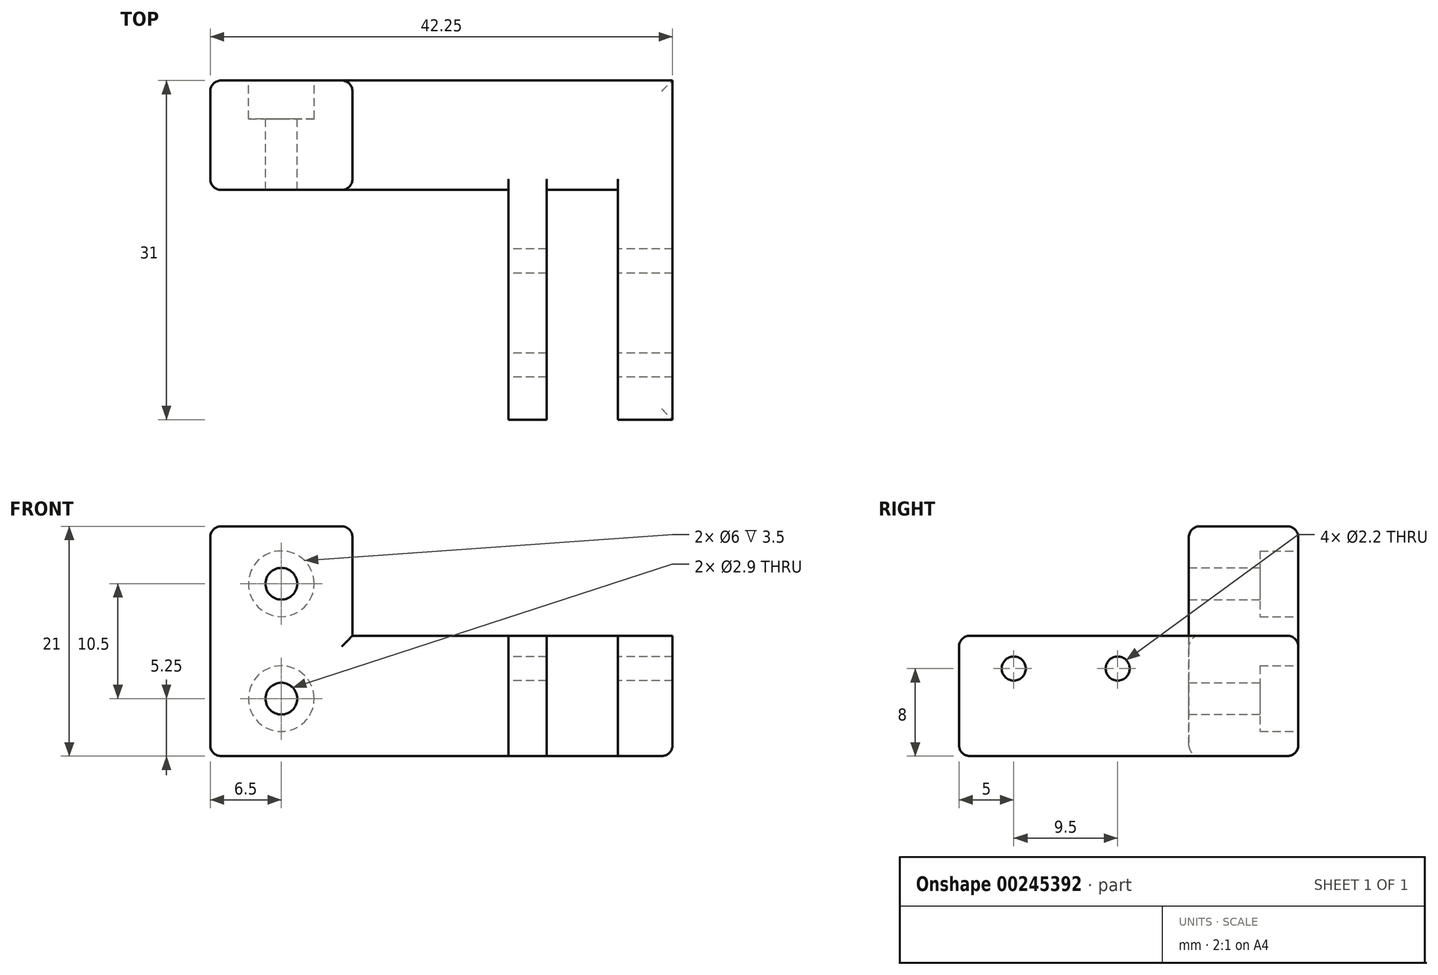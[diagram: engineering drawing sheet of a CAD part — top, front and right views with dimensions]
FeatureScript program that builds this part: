
annotation { "Feature Type Name" : "Feature", "Feature Type Description" : "" }
export const myFeature = defineFeature(function(context is Context, id is Id, definition is map)
    precondition{}
    {
        {
            var Q0;
            Q0=qCreatedBy(makeId("Front.planeOp"),FACE);
            var sketch = newSketch(context, id + "F0", { "sketchPlane" : qUnion([Q0])});
            skLineSegment(sketch, "E0.bottom", {"start": v(0, 0) * mm, "end": v(16.5, 0) * mm});
            skLineSegment(sketch, "E0.top", {"start": v(0, 11) * mm, "end": v(16.5, 11) * mm});
            skLineSegment(sketch, "E0.left", {"start": v(0, 0) * mm, "end": v(0, 11) * mm});
            skLineSegment(sketch, "E0.right", {"start": v(16.5, 0) * mm, "end": v(16.5, 11) * mm});
            skSolve(sketch);
        }
        {
            var Q0;
            Q0=qSketchRegion(id+"F0",true);
            extrude(context, id + "F1", {"entities" : qUnion([Q0]), "depth" : 10 * mm});
        }
        {
            var Q0;
            Q0=makeQuery(id+"F1.opExtrude","CAP_FACE",FACE,{"disambiguationData":[OSD([sQuery(id+"F0.wireOp",EDGE,"E0.bottom"),sQuery(id+"F0.wireOp",EDGE,"E0.top"),sQuery(id+"F0.wireOp",EDGE,"E0.left"),sQuery(id+"F0.wireOp",EDGE,"E0.right")])],"isStart":false});
            var sketch = newSketch(context, id + "F2", { "sketchPlane" : qUnion([Q0])});
            skLineSegment(sketch, "E1.left", {"start": v(11.5, 11) * mm, "end": v(11.5, 0) * mm});
            skLineSegment(sketch, "E1.right", {"start": v(5, 11) * mm, "end": v(5, 0) * mm});
            skPoint(sketch, "E1.middle", {"position": v(8.25, 5.5) * mm});
            skPoint(sketch, "E1.middle.positionSnap0", {"position": v(0, 5.5) * mm});
            skPoint(sketch, "E1.middle.positionSnap1", {"position": v(8.25, 0) * mm});
            skPoint(sketch, "E1.centerSnap0", {"position": v(0, 5.5) * mm});
            skPoint(sketch, "E1.centerSnap1", {"position": v(8.25, 0) * mm});
            skLineSegment(sketch, "E2", {"start": v(5, 11) * mm, "end": v(0, 11) * mm});
            skLineSegment(sketch, "E3", {"start": v(0, 11) * mm, "end": v(0, 0) * mm});
            skLineSegment(sketch, "E4", {"start": v(0, 0) * mm, "end": v(5, 0) * mm});
            skLineSegment(sketch, "E5", {"start": v(11.5, 11) * mm, "end": v(16.5, 11) * mm});
            skLineSegment(sketch, "E6", {"start": v(16.5, 11) * mm, "end": v(16.5, 0) * mm});
            skLineSegment(sketch, "E7", {"start": v(16.5, 0) * mm, "end": v(11.5, 0) * mm});
            skSolve(sketch);
        }
        {
            var Q0;
            Q0=qSketchRegion(id+"F2",true);
            extrude(context, id + "F3", {"entities" : qUnion([Q0]), "operationType" : NewBodyOperationType.ADD, "depth" : 21 * mm});
        }
        {
            var Q0;
            Q0=makeQuery(id+"F3.boolean.opBoolean","MERGE",FACE,{"derivedFrom":[makeQuery(id+"F1.opExtrude","SWEPT_FACE",FACE,{"disambiguationData":[OSD([sQuery(id+"F0.wireOp",EDGE,"E0.left")])]}),makeQuery(id+"F3.opExtrude","SWEPT_FACE",FACE,{"disambiguationData":[OSD([sQuery(id+"F2.wireOp",EDGE,"E3")])]})]});
            var sketch = newSketch(context, id + "F4", { "sketchPlane" : qUnion([Q0])});
            skLineSegment(sketch, "E8", {"start": v(31, 11) * mm, "end": v(31, 8) * mm});
            skLineSegment(sketch, "E9", {"start": v(31, 8) * mm, "end": v(26, 8) * mm});
            skCircle(sketch, "E10", {"center": v(26, 8) * mm, "radius": 1.1 * mm});
            skLineSegment(sketch, "E11", {"start": v(26, 8) * mm, "end": v(16.5, 8) * mm});
            skCircle(sketch, "E12", {"center": v(16.5, 8) * mm, "radius": 1.1 * mm});
            skSolve(sketch);
        }
        {
            var Q0;
            Q0=qSketchRegion(id+"F4",true);
            extrude(context, id + "F5", {"entities" : qUnion([Q0]), "operationType" : NewBodyOperationType.REMOVE, "oppositeDirection" : true, "depth" : 25 * mm});
        }
        {
            var Q0;
            Q0=makeQuery(id+"F3.opExtrude","CAP_FACE",FACE,{"disambiguationData":[OSD([sQuery(id+"F2.wireOp",EDGE,"E1.right"),sQuery(id+"F2.wireOp",EDGE,"E2"),sQuery(id+"F2.wireOp",EDGE,"E3"),sQuery(id+"F2.wireOp",EDGE,"E4")])],"isStart":false});
            var sketch = newSketch(context, id + "F6", { "sketchPlane" : qUnion([Q0])});
            skLineSegment(sketch, "E13", {"start": v(0, 0) * mm, "end": v(8.25, 0) * mm});
            skLineSegment(sketch, "E14", {"start": v(8.25, 0) * mm, "end": v(-2.25, 0) * mm});
            skLineSegment(sketch, "E15", {"start": v(-2.25, 0) * mm, "end": v(1.5, 0) * mm});
            skLineSegment(sketch, "E16", {"start": v(5, 0) * mm, "end": v(1.5, 0) * mm});
            skLineSegment(sketch, "E17.bottom", {"start": v(0, 0) * mm, "end": v(1.5, 0) * mm});
            skLineSegment(sketch, "E17.top", {"start": v(0, 11) * mm, "end": v(1.5, 11) * mm});
            skLineSegment(sketch, "E17.left", {"start": v(0, 0) * mm, "end": v(0, 11) * mm});
            skLineSegment(sketch, "E17.right", {"start": v(1.5, 0) * mm, "end": v(1.5, 11) * mm});
            skSolve(sketch);
        }
        {
            var Q0;
            Q0=qSketchRegion(id+"F6",true);
            extrude(context, id + "F7", {"entities" : qUnion([Q0]), "operationType" : NewBodyOperationType.REMOVE, "oppositeDirection" : true, "depth" : 21 * mm});
        }
        {
            var Q0;
            Q0=makeQuery(id+"F3.boolean.opBoolean","MERGE",FACE,{"derivedFrom":[makeQuery(id+"F1.opExtrude","SWEPT_FACE",FACE,{"disambiguationData":[OSD([sQuery(id+"F0.wireOp",EDGE,"E0.left")])]}),makeQuery(id+"F3.opExtrude","SWEPT_FACE",FACE,{"disambiguationData":[OSD([sQuery(id+"F2.wireOp",EDGE,"E3")])]})]});
            extrude(context, id + "F8", {"entities" : qUnion([Q0]), "operationType" : NewBodyOperationType.ADD, "depth" : (34 - 8.25) * mm});
        }
        {
            var Q0;
            {var subQ0=sQuery(id+"F2.wireOp",EDGE,"E2");var subQ1=sQuery(id+"F0.wireOp",EDGE,"E0.top");Q0=makeQuery(id+"F8.boolean.opBoolean","MERGE",FACE,{"derivedFrom":[makeQuery(id+"F3.boolean.opBoolean","MERGE",FACE,{"derivedFrom":[makeQuery(id+"F1.opExtrude","SWEPT_FACE",FACE,{"disambiguationData":[OSD([subQ1])]}),makeQuery(id+"F3.opExtrude","SWEPT_FACE",FACE,{"disambiguationData":[OSD([subQ0])]}),makeQuery(id+"F3.opExtrude","SWEPT_FACE",FACE,{"disambiguationData":[OSD([sQuery(id+"F2.wireOp",EDGE,"E5")])]})]}),makeQuery(id+"F8.opExtrude","SWEPT_FACE",FACE,{"disambiguationData":[OSD([subQ1,sQuery(id+"F0.wireOp",EDGE,"E0.left"),subQ0,sQuery(id+"F2.wireOp",EDGE,"E3")])]})]});}
            var sketch = newSketch(context, id + "F9", { "sketchPlane" : qUnion([Q0])});
            skLineSegment(sketch, "E18.bottom", {"start": v(-25.75, 0) * mm, "end": v(-12.75, 0) * mm});
            skLineSegment(sketch, "E18.top", {"start": v(-25.75, -10) * mm, "end": v(-12.75, -10) * mm});
            skLineSegment(sketch, "E18.left", {"start": v(-25.75, 0) * mm, "end": v(-25.75, -10) * mm});
            skLineSegment(sketch, "E18.right", {"start": v(-12.75, 0) * mm, "end": v(-12.75, -10) * mm});
            skSolve(sketch);
        }
        {
            var Q0;
            Q0=qSketchRegion(id+"F9",true);
            extrude(context, id + "F10", {"entities" : qUnion([Q0]), "operationType" : NewBodyOperationType.ADD, "depth" : 10 * mm});
        }
        {
            var Q0;
            {var subQ0=sQuery(id+"F0.wireOp",EDGE,"E0.left");Q0=makeQuery(id+"F10.boolean.opBoolean","MERGE",FACE,{"derivedFrom":[makeQuery(id+"F8.boolean.opBoolean","MERGE",FACE,{"derivedFrom":[makeQuery(id+"F1.opExtrude","CAP_FACE",FACE,{"disambiguationData":[OSD([sQuery(id+"F0.wireOp",EDGE,"E0.bottom"),sQuery(id+"F0.wireOp",EDGE,"E0.top"),subQ0,sQuery(id+"F0.wireOp",EDGE,"E0.right")])],"isStart":true}),makeQuery(id+"F8.opExtrude","SWEPT_FACE",FACE,{"disambiguationData":[OSD([subQ0])]})]}),makeQuery(id+"F10.opExtrude","SWEPT_FACE",FACE,{"disambiguationData":[OSD([sQuery(id+"F9.wireOp",EDGE,"E18.bottom")])]})]});}
            var sketch = newSketch(context, id + "F11", { "sketchPlane" : qUnion([Q0])});
            skLineSegment(sketch, "E19", {"start": v(19.25, 21) * mm, "end": v(19.25, 10.5) * mm});
            skLineSegment(sketch, "E20", {"start": v(19.25, 10.5) * mm, "end": v(25.24, 10.5) * mm});
            skPoint(sketch, "E21.orphan", {"position": v(19.25, 0) * mm});
            skCircle(sketch, "E22", {"center": v(19.25, 15.75) * mm, "radius": 3 * mm});
            skCircle(sketch, "E23.MirrorC", {"center": v(19.25, 5.25) * mm, "radius": 3 * mm});
            skSolve(sketch);
        }
        {
            var Q0;
            Q0=qSketchRegion(id+"F11",true);
            extrude(context, id + "F12", {"entities" : qUnion([Q0]), "operationType" : NewBodyOperationType.REMOVE, "oppositeDirection" : true, "depth" : 3.5 * mm});
        }
        {
            var Q0;
            {var subQ0=sQuery(id+"F0.wireOp",EDGE,"E0.left");Q0=makeQuery(id+"F10.boolean.opBoolean","MERGE",FACE,{"derivedFrom":[makeQuery(id+"F8.boolean.opBoolean","MERGE",FACE,{"derivedFrom":[makeQuery(id+"F1.opExtrude","CAP_FACE",FACE,{"disambiguationData":[OSD([sQuery(id+"F0.wireOp",EDGE,"E0.bottom"),sQuery(id+"F0.wireOp",EDGE,"E0.top"),subQ0,sQuery(id+"F0.wireOp",EDGE,"E0.right")])],"isStart":true}),makeQuery(id+"F8.opExtrude","SWEPT_FACE",FACE,{"disambiguationData":[OSD([subQ0])]})]}),makeQuery(id+"F10.opExtrude","SWEPT_FACE",FACE,{"disambiguationData":[OSD([sQuery(id+"F9.wireOp",EDGE,"E18.bottom")])]})]});}
            var sketch = newSketch(context, id + "F13", { "sketchPlane" : qUnion([Q0])});
            skCircle(sketch, "E24", {"center": v(19.25, 15.75) * mm, "radius": 1.45 * mm});
            skCircle(sketch, "E25", {"center": v(19.25, 5.25) * mm, "radius": 1.45 * mm});
            skSolve(sketch);
        }
        {
            var Q0;
            Q0=qSketchRegion(id+"F13",true);
            extrude(context, id + "F14", {"entities" : qUnion([Q0]), "operationType" : NewBodyOperationType.REMOVE, "oppositeDirection" : true, "depth" : 25 * mm});
        }
        {
            var Q0;
            Q0=makeQuery(id+"F10.opExtrude","CAP_EDGE",EDGE,{"disambiguationData":[OSD([sQuery(id+"F9.wireOp",EDGE,"E18.right")])],"isStart":false});
            var Q1;
            Q1=makeQuery(id+"F10.opExtrude","CAP_EDGE",EDGE,{"disambiguationData":[OSD([sQuery(id+"F9.wireOp",EDGE,"E18.left")])],"isStart":false});
            var Q2;
            Q2=makeQuery(id+"F10.opExtrude","CAP_EDGE",EDGE,{"disambiguationData":[OSD([sQuery(id+"F9.wireOp",EDGE,"E18.bottom")])],"isStart":false});
            var Q3;
            Q3=makeQuery(id+"F10.boolean.opBoolean","MERGE",EDGE,{"derivedFrom":[makeQuery(id+"F8.opExtrude","CAP_EDGE",EDGE,{"disambiguationData":[OSD([sQuery(id+"F0.wireOp",EDGE,"E0.left")])],"isStart":false}),makeQuery(id+"F10.opExtrude","SWEPT_EDGE",EDGE,{"disambiguationData":[OSD([sQuery(id+"F9.wireOp",EDGE,"E18.bottom"),sQuery(id+"F9.wireOp",EDGE,"E18.left")])]})]});
            var Q4;
            Q4=makeQuery(id+"F10.boolean.opBoolean","MERGE",EDGE,{"derivedFrom":[makeQuery(id+"F8.opExtrude","CAP_EDGE",EDGE,{"disambiguationData":[OSD([sQuery(id+"F6.wireOp",EDGE,"E17.left")])],"isStart":false}),makeQuery(id+"F10.opExtrude","SWEPT_EDGE",EDGE,{"disambiguationData":[OSD([sQuery(id+"F9.wireOp",EDGE,"E18.top"),sQuery(id+"F9.wireOp",EDGE,"E18.left")])]})]});
            var Q5;
            Q5=makeQuery(id+"F8.opExtrude","CAP_EDGE",EDGE,{"disambiguationData":[OSD([sQuery(id+"F0.wireOp",EDGE,"E0.bottom"),sQuery(id+"F0.wireOp",EDGE,"E0.left"),sQuery(id+"F2.wireOp",EDGE,"E3"),sQuery(id+"F2.wireOp",EDGE,"E4")])],"isStart":false});
            var Q6;
            {var subQ0=sQuery(id+"F0.wireOp",EDGE,"E0.bottom");Q6=makeQuery(id+"F8.boolean.opBoolean","MERGE",EDGE,{"derivedFrom":[makeQuery(id+"F1.opExtrude","CAP_EDGE",EDGE,{"disambiguationData":[OSD([subQ0])],"isStart":true}),makeQuery(id+"F8.opExtrude","SWEPT_EDGE",EDGE,{"disambiguationData":[OSD([subQ0,sQuery(id+"F0.wireOp",EDGE,"E0.left")])]})]});}
            var Q7;
            {var subQ0=sQuery(id+"F6.wireOp",EDGE,"E17.bottom");Q7=makeQuery(id+"F8.boolean.opBoolean","MERGE",EDGE,{"derivedFrom":[makeQuery(id+"F7.boolean.opBoolean","COPY",EDGE,{"derivedFrom":makeQuery(id+"F7.opExtrude","CAP_EDGE",EDGE,{"disambiguationData":[OSD([subQ0])],"isStart":false})}),makeQuery(id+"F8.opExtrude","SWEPT_EDGE",EDGE,{"disambiguationData":[OSD([subQ0,sQuery(id+"F6.wireOp",EDGE,"E17.left")])]})]});}
            var Q8;
            Q8=makeQuery(id+"F10.opExtrude","SWEPT_EDGE",EDGE,{"disambiguationData":[OSD([sQuery(id+"F0.wireOp",EDGE,"E0.top"),sQuery(id+"F0.wireOp",EDGE,"E0.left"),sQuery(id+"F9.wireOp",EDGE,"E18.bottom"),sQuery(id+"F9.wireOp",EDGE,"E18.right")])]});
            var Q9;
            Q9=makeQuery(id+"F10.opExtrude","SWEPT_EDGE",EDGE,{"disambiguationData":[OSD([sQuery(id+"F6.wireOp",EDGE,"E17.top"),sQuery(id+"F6.wireOp",EDGE,"E17.left"),sQuery(id+"F9.wireOp",EDGE,"E18.top"),sQuery(id+"F9.wireOp",EDGE,"E18.right")])]});
            var Q10;
            {var subQ0=sQuery(id+"F0.wireOp",EDGE,"E0.top");Q10=makeQuery(id+"F8.boolean.opBoolean","MERGE",EDGE,{"derivedFrom":[makeQuery(id+"F1.opExtrude","CAP_EDGE",EDGE,{"disambiguationData":[OSD([subQ0])],"isStart":true}),makeQuery(id+"F8.opExtrude","SWEPT_EDGE",EDGE,{"disambiguationData":[OSD([subQ0,sQuery(id+"F0.wireOp",EDGE,"E0.left")])]})]});}
            var Q11;
            {var subQ0=sQuery(id+"F6.wireOp",EDGE,"E17.top");Q11=makeQuery(id+"F8.boolean.opBoolean","MERGE",EDGE,{"derivedFrom":[makeQuery(id+"F7.boolean.opBoolean","COPY",EDGE,{"derivedFrom":makeQuery(id+"F7.opExtrude","CAP_EDGE",EDGE,{"disambiguationData":[OSD([subQ0])],"isStart":false})}),makeQuery(id+"F8.opExtrude","SWEPT_EDGE",EDGE,{"disambiguationData":[OSD([subQ0,sQuery(id+"F6.wireOp",EDGE,"E17.left")])]})]});}
            var Q12;
            Q12=makeQuery(id+"F1.opExtrude","CAP_EDGE",EDGE,{"disambiguationData":[OSD([sQuery(id+"F0.wireOp",EDGE,"E0.top")])],"isStart":false});
            var Q13;
            Q13=makeQuery(id+"F1.opExtrude","CAP_EDGE",EDGE,{"disambiguationData":[OSD([sQuery(id+"F0.wireOp",EDGE,"E0.bottom")])],"isStart":false});
            var Q14;
            Q14=makeQuery(id+"F3.opExtrude","CAP_EDGE",EDGE,{"disambiguationData":[OSD([sQuery(id+"F2.wireOp",EDGE,"E2")])],"isStart":false});
            var Q15;
            Q15=makeQuery(id+"F3.opExtrude","CAP_EDGE",EDGE,{"disambiguationData":[OSD([sQuery(id+"F2.wireOp",EDGE,"E5")])],"isStart":false});
            var Q16;
            Q16=makeQuery(id+"F3.opExtrude","CAP_EDGE",EDGE,{"disambiguationData":[OSD([sQuery(id+"F2.wireOp",EDGE,"E7")])],"isStart":false});
            var Q17;
            Q17=makeQuery(id+"F3.boolean.opBoolean","MERGE",EDGE,{"derivedFrom":[makeQuery(id+"F1.opExtrude","SWEPT_EDGE",EDGE,{"disambiguationData":[OSD([sQuery(id+"F0.wireOp",EDGE,"E0.bottom"),sQuery(id+"F0.wireOp",EDGE,"E0.right")])]}),makeQuery(id+"F3.opExtrude","SWEPT_EDGE",EDGE,{"disambiguationData":[OSD([sQuery(id+"F2.wireOp",EDGE,"E6"),sQuery(id+"F2.wireOp",EDGE,"E7")])]})]});
            var Q18;
            Q18=makeQuery(id+"F3.opExtrude","CAP_EDGE",EDGE,{"disambiguationData":[OSD([sQuery(id+"F2.wireOp",EDGE,"E4")])],"isStart":false});
            fillet(context, id + "F15", {"entities" : qUnion([Q0, Q1, Q2, Q3, Q4, Q5, Q6, Q7, Q8, Q9, Q10, Q11, Q12, Q13, Q14, Q15, Q16, Q17, Q18]), "radius" : 1 * mm, "tangentPropagation" : true, "allowEdgeOverflow" : false});
        }
        {
            var Q0;
            Q0=makeQuery(id+"F10.opExtrude","CAP_EDGE",EDGE,{"disambiguationData":[OSD([sQuery(id+"F9.wireOp",EDGE,"E18.top")])],"isStart":false});
            fillet(context, id + "F16", {"entities" : qUnion([Q0]), "radius" : 1 * mm, "tangentPropagation" : true, "allowEdgeOverflow" : false});
        }
    });
